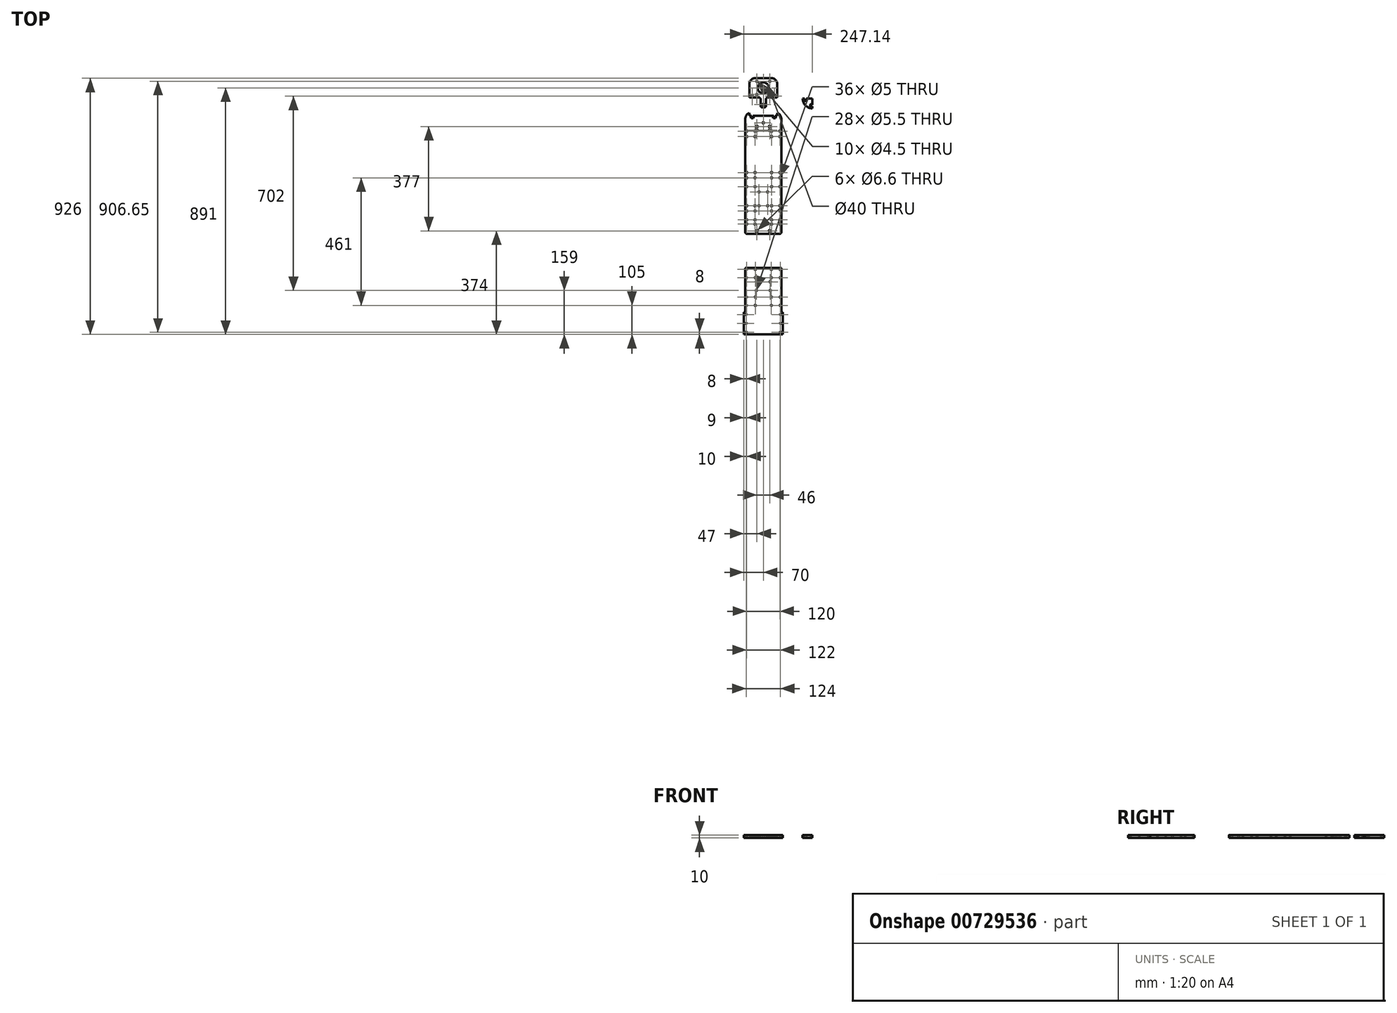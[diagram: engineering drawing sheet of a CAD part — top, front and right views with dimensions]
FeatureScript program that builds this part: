
annotation { "Feature Type Name" : "Feature", "Feature Type Description" : "" }
export const myFeature = defineFeature(function(context is Context, id is Id, definition is map)
    precondition{}
    {
        {
            var Q0;
            Q0=qCreatedBy(makeId("Top.planeOp"),FACE);
            var sketch = newSketch(context, id + "F0", { "sketchPlane" : qUnion([Q0])});
            skLineSegment(sketch, "E0.bottom", {"start": v(-65, 200) * mm, "end": v(65, 200) * mm});
            skLineSegment(sketch, "E0.top", {"start": v(-65, -200) * mm, "end": v(65, -200) * mm});
            skLineSegment(sketch, "E0.left", {"start": v(-65, 200) * mm, "end": v(-65, -121) * mm});
            skLineSegment(sketch, "E0.right", {"start": v(65, 200) * mm, "end": v(65, -121) * mm});
            skLineSegment(sketch, "E1", {"start": v(0, 0) * mm, "end": v(370.23, 0) * mm, "construction": true});
            skLineSegment(sketch, "E2", {"start": v(0, 0) * mm, "end": v(0, -200) * mm, "construction": true});
            skLineSegment(sketch, "E3", {"start": v(45, 0) * mm, "end": v(45, -60) * mm, "construction": true});
            skLineSegment(sketch, "E4", {"start": v(45, -60) * mm, "end": v(30.89, -60) * mm, "construction": true});
            skLineSegment(sketch, "E5", {"start": v(45, -44) * mm, "end": v(30, -44) * mm, "construction": true});
            skCircle(sketch, "E6", {"center": v(30, -44) * mm, "radius": 2.5 * mm});
            skCircle(sketch, "E7.MirrorC", {"center": v(30, -76) * mm, "radius": 2.5 * mm});
            skCircle(sketch, "E8.MirrorC", {"center": v(60, -44) * mm, "radius": 2.5 * mm});
            skCircle(sketch, "E9.MirrorC", {"center": v(60, -76) * mm, "radius": 2.5 * mm});
            skCircle(sketch, "E10.MirrorC", {"center": v(30, 44) * mm, "radius": 2.5 * mm});
            skCircle(sketch, "E11.MirrorC", {"center": v(60, 44) * mm, "radius": 2.5 * mm});
            skCircle(sketch, "E12.MirrorC", {"center": v(60, 76) * mm, "radius": 2.5 * mm});
            skCircle(sketch, "E13.MirrorC", {"center": v(30, 76) * mm, "radius": 2.5 * mm});
            skCircle(sketch, "E14.MirrorC", {"center": v(-30, 76) * mm, "radius": 2.5 * mm});
            skCircle(sketch, "E15.MirrorC", {"center": v(-30, 44) * mm, "radius": 2.5 * mm});
            skCircle(sketch, "E16.MirrorC", {"center": v(-60, 76) * mm, "radius": 2.5 * mm});
            skCircle(sketch, "E17.MirrorC", {"center": v(-60, 44) * mm, "radius": 2.5 * mm});
            skCircle(sketch, "E18.MirrorC", {"center": v(-60, -44) * mm, "radius": 2.5 * mm});
            skCircle(sketch, "E19.MirrorC", {"center": v(-30, -44) * mm, "radius": 2.5 * mm});
            skCircle(sketch, "E20.MirrorC", {"center": v(-30, -76) * mm, "radius": 2.5 * mm});
            skCircle(sketch, "E21.MirrorC", {"center": v(-60, -76) * mm, "radius": 2.5 * mm});
            skLineSegment(sketch, "E22", {"start": v(-131.72, 0) * mm, "end": v(0, 0) * mm, "construction": true});
            skPoint(sketch, "E23.orphan", {"position": v(65, 0) * mm});
            skCircle(sketch, "E24", {"center": v(-60, -55) * mm, "radius": 2.75 * mm, "construction": true});
            skLineSegment(sketch, "E25", {"start": v(-60, -55) * mm, "end": v(-30, -55) * mm, "construction": true});
            skLineSegment(sketch, "E26", {"start": v(-45, -390) * mm, "end": v(-45, -55) * mm, "construction": true});
            skCircle(sketch, "E27.MirrorC", {"center": v(-30, -55) * mm, "radius": 2.75 * mm, "construction": true});
            skCircle(sketch, "E28.0.1.0", {"center": v(-60, 95) * mm, "radius": 2.75 * mm});
            skCircle(sketch, "E28.0.1.1", {"center": v(-30, 95) * mm, "radius": 2.75 * mm});
            skCircle(sketch, "E28.0.2.0", {"center": v(-60, 245) * mm, "radius": 2.75 * mm});
            skCircle(sketch, "E28.0.2.1", {"center": v(-30, 245) * mm, "radius": 2.75 * mm});
            skCircle(sketch, "E28.1.0.0", {"center": v(30, -55) * mm, "radius": 2.75 * mm, "construction": true});
            skCircle(sketch, "E28.1.0.1", {"center": v(60, -55) * mm, "radius": 2.75 * mm, "construction": true});
            skCircle(sketch, "E28.1.1.0", {"center": v(30, 95) * mm, "radius": 2.75 * mm});
            skCircle(sketch, "E28.1.1.1", {"center": v(60, 95) * mm, "radius": 2.75 * mm});
            skCircle(sketch, "E28.1.2.0", {"center": v(30, 245) * mm, "radius": 2.75 * mm});
            skCircle(sketch, "E28.1.2.1", {"center": v(60, 245) * mm, "radius": 2.75 * mm});
            skLineSegment(sketch, "E28.direction1", {"start": v(-60, -55) * mm, "end": v(30, -55) * mm, "construction": true});
            skLineSegment(sketch, "E28.direction2", {"start": v(-60, -55) * mm, "end": v(-60, 95) * mm, "construction": true});
            skLineSegment(sketch, "E29", {"start": v(-65, -200) * mm, "end": v(-65, -250) * mm, "construction": true});
            skLineSegment(sketch, "E30", {"start": v(65, -200) * mm, "end": v(65, -250) * mm, "construction": true});
            skLineSegment(sketch, "E31.bottom", {"start": v(-65, -250) * mm, "end": v(65, -250) * mm});
            skLineSegment(sketch, "E31.top", {"start": v(-65, -390) * mm, "end": v(65, -390) * mm});
            skLineSegment(sketch, "E31.left", {"start": v(-65, -250) * mm, "end": v(-65, -390) * mm});
            skLineSegment(sketch, "E31.right", {"start": v(65, -250) * mm, "end": v(65, -390) * mm});
            skLineSegment(sketch, "E32", {"start": v(-65, -320) * mm, "end": v(65, -320) * mm, "construction": true});
            skPoint(sketch, "E33.orphan", {"position": v(-45, -52) * mm});
            skLineSegment(sketch, "E34", {"start": v(-45, -270) * mm, "end": v(-55, -270) * mm, "construction": true});
            skCircle(sketch, "E35", {"center": v(-61, -255) * mm, "radius": 2.5 * mm});
            skCircle(sketch, "E36.MirrorC", {"center": v(-61, -285) * mm, "radius": 2.5 * mm});
            skCircle(sketch, "E37.MirrorC", {"center": v(-29, -255) * mm, "radius": 2.5 * mm});
            skCircle(sketch, "E38.MirrorC", {"center": v(-29, -285) * mm, "radius": 2.5 * mm});
            skLineSegment(sketch, "E39", {"start": v(0, -320) * mm, "end": v(0, -250) * mm, "construction": true});
            skCircle(sketch, "E40.MirrorC", {"center": v(-29, -355) * mm, "radius": 2.5 * mm});
            skCircle(sketch, "E41.MirrorC", {"center": v(-61, -355) * mm, "radius": 2.5 * mm});
            skCircle(sketch, "E42.MirrorC", {"center": v(-61, -385) * mm, "radius": 2.5 * mm});
            skCircle(sketch, "E43.MirrorC", {"center": v(-29, -385) * mm, "radius": 2.5 * mm});
            skCircle(sketch, "E44.MirrorC", {"center": v(29, -255) * mm, "radius": 2.5 * mm});
            skCircle(sketch, "E45.MirrorC", {"center": v(29, -285) * mm, "radius": 2.5 * mm});
            skCircle(sketch, "E46.MirrorC", {"center": v(61, -255) * mm, "radius": 2.5 * mm});
            skCircle(sketch, "E47.MirrorC", {"center": v(61, -285) * mm, "radius": 2.5 * mm});
            skCircle(sketch, "E48.MirrorC", {"center": v(29, -355) * mm, "radius": 2.5 * mm});
            skCircle(sketch, "E49.MirrorC", {"center": v(61, -355) * mm, "radius": 2.5 * mm});
            skCircle(sketch, "E50.MirrorC", {"center": v(61, -385) * mm, "radius": 2.5 * mm});
            skCircle(sketch, "E51.MirrorC", {"center": v(29, -385) * mm, "radius": 2.5 * mm});
            skLineSegment(sketch, "E52.top", {"start": v(-65, -490) * mm, "end": v(65, -490) * mm});
            skLineSegment(sketch, "E52.left", {"start": v(-65, -390) * mm, "end": v(-65, -490) * mm});
            skLineSegment(sketch, "E52.right", {"start": v(65, -390) * mm, "end": v(65, -490) * mm});
            skLineSegment(sketch, "E53.top", {"start": v(-55, 300) * mm, "end": v(55, 300) * mm});
            skLineSegment(sketch, "E53.left", {"start": v(-65, 200) * mm, "end": v(-65, 290) * mm});
            skLineSegment(sketch, "E53.right", {"start": v(65, 200) * mm, "end": v(65, 290) * mm});
            skLineSegment(sketch, "E54", {"start": v(-60, -126) * mm, "end": v(60, -126) * mm});
            skPoint(sketch, "E55.middle", {"position": v(0, 0) * mm});
            skLineSegment(sketch, "E56.bottom", {"start": v(15.5, 25) * mm, "end": v(-15.5, 25) * mm, "construction": true});
            skLineSegment(sketch, "E56.top", {"start": v(15.5, -25) * mm, "end": v(-15.5, -25) * mm, "construction": true});
            skLineSegment(sketch, "E56.left", {"start": v(15.5, 25) * mm, "end": v(15.5, -25) * mm, "construction": true});
            skLineSegment(sketch, "E56.right", {"start": v(-15.5, 25) * mm, "end": v(-15.5, -25) * mm, "construction": true});
            skCircle(sketch, "E57", {"center": v(-15.5, 25) * mm, "radius": 2.5 * mm});
            skPoint(sketch, "E58.orphan", {"position": v(-65, 0) * mm});
            skLineSegment(sketch, "E59", {"start": v(0, 0) * mm, "end": v(0, 25) * mm, "construction": true});
            skCircle(sketch, "E60.MirrorC", {"center": v(15.5, 25) * mm, "radius": 2.5 * mm});
            skCircle(sketch, "E61.MirrorC", {"center": v(15.5, -25) * mm, "radius": 2.5 * mm});
            skCircle(sketch, "E62.MirrorC", {"center": v(-15.5, -25) * mm, "radius": 2.5 * mm});
            skLineSegment(sketch, "E63.bottom", {"start": v(-30, 30) * mm, "end": v(30, 30) * mm, "construction": true});
            skLineSegment(sketch, "E63.top", {"start": v(-30, -30) * mm, "end": v(30, -30) * mm, "construction": true});
            skLineSegment(sketch, "E63.left", {"start": v(-30, 30) * mm, "end": v(-30, -30) * mm, "construction": true});
            skLineSegment(sketch, "E63.right", {"start": v(30, 30) * mm, "end": v(30, -30) * mm, "construction": true});
            skLineSegment(sketch, "E64", {"start": v(0, -116) * mm, "end": v(23, -116) * mm, "construction": true});
            skCircle(sketch, "E65", {"center": v(23, -116) * mm, "radius": 3.3 * mm});
            skCircle(sketch, "E66.MirrorC", {"center": v(-23, -116) * mm, "radius": 3.3 * mm});
            skCircle(sketch, "E67", {"center": v(-25, -300) * mm, "radius": 2.75 * mm});
            skCircle(sketch, "E68.0.1.0", {"center": v(-25, -331) * mm, "radius": 2.75 * mm});
            skCircle(sketch, "E68.1.0.0", {"center": v(25, -300) * mm, "radius": 2.75 * mm});
            skCircle(sketch, "E68.1.1.0", {"center": v(25, -331) * mm, "radius": 2.75 * mm});
            skLineSegment(sketch, "E68.direction1", {"start": v(-25, -300) * mm, "end": v(25, -300) * mm, "construction": true});
            skLineSegment(sketch, "E68.direction2", {"start": v(-25, -300) * mm, "end": v(-25, -331) * mm, "construction": true});
            skLineSegment(sketch, "E69.bottom", {"start": v(70, -490) * mm, "end": v(-70, -490) * mm});
            skLineSegment(sketch, "E69.top", {"start": v(70, -410) * mm, "end": v(-70, -410) * mm});
            skLineSegment(sketch, "E69.left", {"start": v(70, -490) * mm, "end": v(70, -410) * mm});
            skLineSegment(sketch, "E69.right", {"start": v(-70, -490) * mm, "end": v(-70, -410) * mm});
            skPoint(sketch, "E69.middle", {"position": v(0, -450) * mm});
            skLineSegment(sketch, "E70", {"start": v(0, 235) * mm, "end": v(0, 333) * mm, "construction": true});
            skLineSegment(sketch, "E71", {"start": v(-65, 235) * mm, "end": v(65, 235) * mm, "construction": true});
            skCircle(sketch, "E72.MirrorC", {"center": v(-60, 225) * mm, "radius": 2.75 * mm});
            skCircle(sketch, "E73.MirrorC", {"center": v(-30, 225) * mm, "radius": 2.75 * mm});
            skCircle(sketch, "E74.MirrorC", {"center": v(30, 225) * mm, "radius": 2.75 * mm});
            skCircle(sketch, "E75.MirrorC", {"center": v(60, 225) * mm, "radius": 2.75 * mm});
            skLineSegment(sketch, "E76.bottom", {"start": v(50, 366) * mm, "end": v(15, 366) * mm});
            skLineSegment(sketch, "E76.top", {"start": v(30, 436) * mm, "end": v(-30, 436) * mm});
            skLineSegment(sketch, "E76.left", {"start": v(50, 366) * mm, "end": v(50, 416) * mm});
            skLineSegment(sketch, "E76.right", {"start": v(-50, 366) * mm, "end": v(-50, 416) * mm});
            skPoint(sketch, "E76.middle", {"position": v(0, 401) * mm});
            skCircle(sketch, "E77", {"center": v(0, 401) * mm, "radius": 20 * mm});
            skLineSegment(sketch, "E78.bottom", {"start": v(-23.65, 424.65) * mm, "end": v(23.65, 424.65) * mm, "construction": true});
            skLineSegment(sketch, "E78.top", {"start": v(-23.65, 377.35) * mm, "end": v(23.65, 377.35) * mm, "construction": true});
            skLineSegment(sketch, "E78.left", {"start": v(-23.65, 424.65) * mm, "end": v(-23.65, 377.35) * mm, "construction": true});
            skLineSegment(sketch, "E78.right", {"start": v(23.65, 424.65) * mm, "end": v(23.65, 377.35) * mm, "construction": true});
            skCircle(sketch, "E79", {"center": v(-23.65, 424.65) * mm, "radius": 2.25 * mm});
            skCircle(sketch, "E80", {"center": v(23.65, 424.65) * mm, "radius": 2.25 * mm});
            skCircle(sketch, "E81", {"center": v(-23.65, 377.35) * mm, "radius": 2.25 * mm});
            skCircle(sketch, "E82", {"center": v(23.65, 377.35) * mm, "radius": 2.25 * mm});
            skLineSegment(sketch, "E83", {"start": v(-40, 292) * mm, "end": v(-40, 300) * mm, "construction": true});
            skLineSegment(sketch, "E84", {"start": v(-40, 292) * mm, "end": v(-36.6, 292) * mm});
            skLineSegment(sketch, "E85", {"start": v(-36.6, 292) * mm, "end": v(-35, 293.6) * mm});
            skLineSegment(sketch, "E86", {"start": v(-35, 293.6) * mm, "end": v(-35, 296) * mm});
            skLineSegment(sketch, "E87", {"start": v(-35, 296) * mm, "end": v(-37, 296) * mm});
            skLineSegment(sketch, "E88", {"start": v(-37, 296) * mm, "end": v(-37, 300) * mm});
            skLineSegment(sketch, "E89", {"start": v(-37, 300) * mm, "end": v(-43, 300) * mm});
            skLineSegment(sketch, "E90", {"start": v(-42.5, 292) * mm, "end": v(-42.5, 300) * mm});
            skLineSegment(sketch, "E91.MirrorCS", {"start": v(-40, 292) * mm, "end": v(-43.4, 292) * mm});
            skLineSegment(sketch, "E92.MirrorCS", {"start": v(-37.5, 292) * mm, "end": v(-37.5, 300) * mm});
            skLineSegment(sketch, "E93.MirrorCS", {"start": v(-43, 300) * mm, "end": v(-37, 300) * mm});
            skLineSegment(sketch, "E94.MirrorCS", {"start": v(-43, 296) * mm, "end": v(-43, 300) * mm});
            skLineSegment(sketch, "E95.MirrorCS", {"start": v(-45, 296) * mm, "end": v(-43, 296) * mm});
            skLineSegment(sketch, "E96.MirrorCS", {"start": v(-45, 293.6) * mm, "end": v(-45, 296) * mm});
            skLineSegment(sketch, "E97.MirrorCS", {"start": v(-43.4, 292) * mm, "end": v(-45, 293.6) * mm});
            skLineSegment(sketch, "E98.MirrorCS", {"start": v(43, 296) * mm, "end": v(43, 300) * mm});
            skLineSegment(sketch, "E99.MirrorCS", {"start": v(45, 296) * mm, "end": v(43, 296) * mm});
            skLineSegment(sketch, "E100.MirrorCS", {"start": v(45, 293.6) * mm, "end": v(45, 296) * mm});
            skLineSegment(sketch, "E101.MirrorCS", {"start": v(43.4, 292) * mm, "end": v(45, 293.6) * mm});
            skLineSegment(sketch, "E102.MirrorCS", {"start": v(40, 292) * mm, "end": v(43.4, 292) * mm});
            skLineSegment(sketch, "E103.MirrorCS", {"start": v(40, 292) * mm, "end": v(36.6, 292) * mm});
            skLineSegment(sketch, "E104.MirrorCS", {"start": v(36.6, 292) * mm, "end": v(35, 293.6) * mm});
            skLineSegment(sketch, "E105.MirrorCS", {"start": v(35, 293.6) * mm, "end": v(35, 296) * mm});
            skLineSegment(sketch, "E106.MirrorCS", {"start": v(35, 296) * mm, "end": v(37, 296) * mm});
            skLineSegment(sketch, "E107.MirrorCS", {"start": v(37, 296) * mm, "end": v(37, 300) * mm});
            skPoint(sketch, "E108.visualSharp", {"position": v(-65, 300) * mm});
            skArc(sketch, "E108.filletArc", {"start": v(-55, 300) * mm, "mid": v(-62.07, 297.07) * mm, "end": v(-65, 290) * mm});
            skPoint(sketch, "E109.visualSharp", {"position": v(65, 300) * mm});
            skArc(sketch, "E109.filletArc", {"start": v(65, 290) * mm, "mid": v(62.07, 297.07) * mm, "end": v(55, 300) * mm});
            skLineSegment(sketch, "E110", {"start": v(-50, 371) * mm, "end": v(50, 371) * mm, "construction": true});
            skCircle(sketch, "E111", {"center": v(40, 371) * mm, "radius": 2.75 * mm});
            skCircle(sketch, "E112.MirrorC", {"center": v(-40, 371) * mm, "radius": 2.75 * mm});
            skLineSegment(sketch, "E113", {"start": v(50, 366) * mm, "end": v(50, 300) * mm, "construction": true});
            skLineSegment(sketch, "E114", {"start": v(50, 300) * mm, "end": v(50, 310) * mm});
            skArc(sketch, "E115", {"start": v(65, 290) * mm, "mid": v(60.83, 302.5) * mm, "end": v(50, 310) * mm});
            skLineSegment(sketch, "E116.MirrorCS", {"start": v(-50, 366) * mm, "end": v(-50, 300) * mm, "construction": true});
            skArc(sketch, "E117.MirrorCS", {"start": v(-65, 290) * mm, "mid": v(-60.83, 302.5) * mm, "end": v(-50, 310) * mm});
            skLineSegment(sketch, "E118.MirrorCS", {"start": v(-50, 300) * mm, "end": v(-50, 310) * mm});
            skPoint(sketch, "E119.orphan", {"position": v(0, 300) * mm});
            skCircle(sketch, "E120", {"center": v(0, 275) * mm, "radius": 2.75 * mm});
            skCircle(sketch, "E121", {"center": v(0, 341) * mm, "radius": 2.75 * mm});
            skPoint(sketch, "E122.visualSharp", {"position": v(-50, 436) * mm});
            skArc(sketch, "E122.filletArc", {"start": v(-30, 436) * mm, "mid": v(-44.14, 430.14) * mm, "end": v(-50, 416) * mm});
            skPoint(sketch, "E123.visualSharp", {"position": v(50, 436) * mm});
            skArc(sketch, "E123.filletArc", {"start": v(50, 416) * mm, "mid": v(44.14, 430.14) * mm, "end": v(30, 436) * mm});
            skLineSegment(sketch, "E124.trimOffspring", {"start": v(0, 333) * mm, "end": v(0, 388.53) * mm, "construction": true});
            skLineSegment(sketch, "E125.top", {"start": v(-5, 331) * mm, "end": v(5, 331) * mm});
            skLineSegment(sketch, "E125.left", {"start": v(-10, 361) * mm, "end": v(-10, 336) * mm});
            skLineSegment(sketch, "E125.right", {"start": v(10, 361) * mm, "end": v(10, 336) * mm});
            skPoint(sketch, "E125.middle", {"position": v(0, 348.5) * mm});
            skPoint(sketch, "E126.visualSharp", {"position": v(-10, 331) * mm});
            skArc(sketch, "E126.filletArc", {"start": v(-10, 336) * mm, "mid": v(-8.54, 332.46) * mm, "end": v(-5, 331) * mm});
            skPoint(sketch, "E127.visualSharp", {"position": v(10, 331) * mm});
            skArc(sketch, "E127.filletArc", {"start": v(5, 331) * mm, "mid": v(8.54, 332.46) * mm, "end": v(10, 336) * mm});
            skLineSegment(sketch, "E128.trimOffspring", {"start": v(-15, 366) * mm, "end": v(-50, 366) * mm});
            skPoint(sketch, "E129.visualSharp", {"position": v(-10, 366) * mm});
            skArc(sketch, "E129.filletArc", {"start": v(-10, 361) * mm, "mid": v(-11.46, 364.54) * mm, "end": v(-15, 366) * mm});
            skPoint(sketch, "E130.visualSharp", {"position": v(10, 366) * mm});
            skArc(sketch, "E130.filletArc", {"start": v(15, 366) * mm, "mid": v(11.46, 364.54) * mm, "end": v(10, 361) * mm});
            skLineSegment(sketch, "E131", {"start": v(152.14, 354.26) * mm, "end": v(152.14, 362.26) * mm, "construction": true});
            skLineSegment(sketch, "E132", {"start": v(152.14, 354.26) * mm, "end": v(155.54, 354.26) * mm});
            skLineSegment(sketch, "E133", {"start": v(155.54, 354.26) * mm, "end": v(157.14, 355.86) * mm});
            skLineSegment(sketch, "E134", {"start": v(157.14, 355.86) * mm, "end": v(157.14, 358.26) * mm});
            skLineSegment(sketch, "E135", {"start": v(157.14, 358.26) * mm, "end": v(155.14, 358.26) * mm});
            skLineSegment(sketch, "E136", {"start": v(155.14, 358.26) * mm, "end": v(155.14, 362.26) * mm});
            skLineSegment(sketch, "E137", {"start": v(155.14, 362.26) * mm, "end": v(149.14, 362.26) * mm});
            skLineSegment(sketch, "E138", {"start": v(149.64, 354.26) * mm, "end": v(149.64, 362.26) * mm});
            skLineSegment(sketch, "E139.MirrorCS", {"start": v(152.14, 354.26) * mm, "end": v(148.74, 354.26) * mm});
            skLineSegment(sketch, "E140.MirrorCS", {"start": v(154.64, 354.26) * mm, "end": v(154.64, 362.26) * mm});
            skLineSegment(sketch, "E141.MirrorCS", {"start": v(149.14, 362.26) * mm, "end": v(155.14, 362.26) * mm});
            skLineSegment(sketch, "E142.MirrorCS", {"start": v(149.14, 358.26) * mm, "end": v(149.14, 362.26) * mm});
            skLineSegment(sketch, "E143.MirrorCS", {"start": v(147.14, 358.26) * mm, "end": v(149.14, 358.26) * mm});
            skLineSegment(sketch, "E144.MirrorCS", {"start": v(147.14, 355.86) * mm, "end": v(147.14, 358.26) * mm});
            skLineSegment(sketch, "E145.MirrorCS", {"start": v(148.74, 354.26) * mm, "end": v(147.14, 355.86) * mm});
            skLineSegment(sketch, "E146", {"start": v(169.14, 337.26) * mm, "end": v(177.14, 337.26) * mm, "construction": true});
            skLineSegment(sketch, "E147", {"start": v(169.14, 337.26) * mm, "end": v(169.14, 333.86) * mm});
            skLineSegment(sketch, "E148", {"start": v(169.14, 333.86) * mm, "end": v(170.74, 332.26) * mm});
            skLineSegment(sketch, "E149", {"start": v(170.74, 332.26) * mm, "end": v(173.14, 332.26) * mm});
            skLineSegment(sketch, "E150", {"start": v(173.14, 332.26) * mm, "end": v(173.14, 334.26) * mm});
            skLineSegment(sketch, "E151", {"start": v(173.14, 334.26) * mm, "end": v(177.14, 334.26) * mm});
            skLineSegment(sketch, "E152", {"start": v(177.14, 334.26) * mm, "end": v(177.14, 340.26) * mm});
            skLineSegment(sketch, "E153", {"start": v(169.14, 339.76) * mm, "end": v(177.14, 339.76) * mm});
            skLineSegment(sketch, "E154.MirrorCS", {"start": v(169.14, 337.26) * mm, "end": v(169.14, 340.66) * mm});
            skLineSegment(sketch, "E155.MirrorCS", {"start": v(169.14, 334.76) * mm, "end": v(177.14, 334.76) * mm});
            skLineSegment(sketch, "E156.MirrorCS", {"start": v(177.14, 340.26) * mm, "end": v(177.14, 334.26) * mm});
            skLineSegment(sketch, "E157.MirrorCS", {"start": v(173.14, 340.26) * mm, "end": v(177.14, 340.26) * mm});
            skLineSegment(sketch, "E158.MirrorCS", {"start": v(173.14, 342.26) * mm, "end": v(173.14, 340.26) * mm});
            skLineSegment(sketch, "E159.MirrorCS", {"start": v(170.74, 342.26) * mm, "end": v(173.14, 342.26) * mm});
            skLineSegment(sketch, "E160.MirrorCS", {"start": v(169.14, 340.66) * mm, "end": v(170.74, 342.26) * mm});
            skLineSegment(sketch, "E161", {"start": v(155.14, 362.26) * mm, "end": v(177.14, 362.26) * mm});
            skLineSegment(sketch, "E162", {"start": v(177.14, 362.26) * mm, "end": v(177.14, 340.26) * mm});
            skLineSegment(sketch, "E163", {"start": v(149.14, 362.26) * mm, "end": v(142.14, 362.26) * mm});
            skLineSegment(sketch, "E164", {"start": v(177.14, 334.26) * mm, "end": v(177.14, 327.26) * mm});
            skArc(sketch, "E165", {"start": v(142.14, 362.26) * mm, "mid": v(152.39, 337.51) * mm, "end": v(177.14, 327.26) * mm});
            skLineSegment(sketch, "E166", {"start": v(-65, -91) * mm, "end": v(65, -91) * mm, "construction": true});
            skLineSegment(sketch, "E167", {"start": v(-8.26, -55) * mm, "end": v(-8.26, -91) * mm, "construction": true});
            skLineSegment(sketch, "E168", {"start": v(-8.26, -73) * mm, "end": v(-15.16, -73) * mm, "construction": true});
            skCircle(sketch, "E169.MirrorC", {"center": v(-30, -91) * mm, "radius": 2.75 * mm});
            skCircle(sketch, "E170.MirrorC", {"center": v(-60, -91) * mm, "radius": 2.75 * mm});
            skCircle(sketch, "E171.MirrorC", {"center": v(30, -91) * mm, "radius": 2.75 * mm});
            skCircle(sketch, "E172.MirrorC", {"center": v(60, -91) * mm, "radius": 2.75 * mm});
            skLineSegment(sketch, "E173", {"start": v(-65, -40) * mm, "end": v(65, -40) * mm, "construction": true});
            skCircle(sketch, "E174.MirrorC", {"center": v(-60, -25) * mm, "radius": 2.75 * mm});
            skCircle(sketch, "E175.MirrorC", {"center": v(-30, -25) * mm, "radius": 2.75 * mm});
            skCircle(sketch, "E176.MirrorC", {"center": v(30, -25) * mm, "radius": 2.75 * mm});
            skCircle(sketch, "E177.MirrorC", {"center": v(60, -25) * mm, "radius": 2.75 * mm});
            skPoint(sketch, "E178.visualSharp", {"position": v(-65, -126) * mm});
            skArc(sketch, "E178.filletArc", {"start": v(-65, -121) * mm, "mid": v(-63.54, -124.54) * mm, "end": v(-60, -126) * mm});
            skPoint(sketch, "E179.visualSharp", {"position": v(65, -126) * mm});
            skArc(sketch, "E179.filletArc", {"start": v(60, -126) * mm, "mid": v(63.54, -124.54) * mm, "end": v(65, -121) * mm});
            skCircle(sketch, "E180", {"center": v(-62, -482) * mm, "radius": 2.25 * mm});
            skCircle(sketch, "E181.0.1.0", {"center": v(-62, -450) * mm, "radius": 2.25 * mm});
            skCircle(sketch, "E181.0.2.0", {"center": v(-62, -418) * mm, "radius": 2.25 * mm});
            skLineSegment(sketch, "E181.direction1", {"start": v(-62, -482) * mm, "end": v(-35, -482) * mm, "construction": true});
            skLineSegment(sketch, "E181.direction2", {"start": v(-62, -482) * mm, "end": v(-62, -450) * mm, "construction": true});
            skCircle(sketch, "E182.MirrorC", {"center": v(62, -418) * mm, "radius": 2.25 * mm});
            skCircle(sketch, "E183.MirrorC", {"center": v(62, -450) * mm, "radius": 2.25 * mm});
            skCircle(sketch, "E184.MirrorC", {"center": v(62, -482) * mm, "radius": 2.25 * mm});
            skLineSegment(sketch, "E185", {"start": v(-23, 261) * mm, "end": v(23, 261) * mm, "construction": true});
            skCircle(sketch, "E186", {"center": v(-23, 261) * mm, "radius": 3.3 * mm});
            skCircle(sketch, "E187.MirrorC", {"center": v(23, 261) * mm, "radius": 3.3 * mm});
            skLineSegment(sketch, "E188", {"start": v(0, 248) * mm, "end": v(23, 248) * mm, "construction": true});
            skCircle(sketch, "E189", {"center": v(23, 248) * mm, "radius": 3.3 * mm});
            skCircle(sketch, "E190.MirrorC", {"center": v(-23, 248) * mm, "radius": 3.3 * mm});
            skSolve(sketch);
        }
        {
            var Q0;
            Q0=makeQuery(id+"F0.imprint","IMPRINT",FACE,{"disambiguationData":[TD([[makeQuery(id+"F0.imprint","IMPRINT",EDGE,{"derivedFrom":sQuery(id+"F0.wireOp",EDGE,"E0.bottom")}),-1.0]])]});
            var Q1;
            Q1=makeQuery(id+"F0.imprint","IMPRINT",FACE,{"disambiguationData":[TD([[makeQuery(id+"F0.imprint","IMPRINT",EDGE,{"derivedFrom":sQuery(id+"F0.wireOp",EDGE,"E0.bottom")}),1.0]])]});
            var Q2;
            Q2=makeQuery(id+"F0.imprint","IMPRINT",FACE,{"disambiguationData":[TD([[makeQuery(id+"F0.imprint","IMPRINT",EDGE,{"derivedFrom":sQuery(id+"F0.wireOp",EDGE,"E0.bottom")}),-1.0]])]});
            var Q3;
            {var subQ5=sQuery(id+"F0.wireOp",EDGE,"E63.right");Q3=makeQuery(id+"F0.imprint","IMPRINT",FACE,{"disambiguationData":[TD([[makeQuery(id+"F0.imprint","IMPRINT",EDGE,{"derivedFrom":subQ5}),-1.0]])]});}
            var Q4;
            {var subQ0=sQuery(id+"F0.wireOp",EDGE,"E108.filletArc");Q4=makeQuery(id+"F0.imprint","IMPRINT",FACE,{"disambiguationData":[TD([[makeQuery(id+"F0.imprint","IMPRINT",EDGE,{"derivedFrom":subQ0}),-1.0]])]});}
            var Q5;
            {var subQ0=sQuery(id+"F0.wireOp",EDGE,"E109.filletArc");Q5=makeQuery(id+"F0.imprint","IMPRINT",FACE,{"disambiguationData":[TD([[makeQuery(id+"F0.imprint","IMPRINT",EDGE,{"derivedFrom":subQ0}),-1.0]])]});}
            extrude(context, id + "F1", {"entities" : qUnion([Q0, Q1, Q2, Q3, Q4, Q5]), "depth" : 10 * mm, "offsetDistance" : 25 * mm});
        }
        {
            var Q0;
            Q0=makeQuery(id+"F0.imprint","IMPRINT",FACE,{"disambiguationData":[TD([[makeQuery(id+"F0.imprint","IMPRINT",EDGE,{"derivedFrom":sQuery(id+"F0.wireOp",EDGE,"E31.bottom")}),-1.0]])]});
            var Q1;
            {var subQ0=sQuery(id+"F0.wireOp",EDGE,"E31.top");Q1=makeQuery(id+"F0.imprint","IMPRINT",FACE,{"disambiguationData":[TD([[makeQuery(id+"F0.imprint","IMPRINT",EDGE,{"derivedFrom":subQ0}),-1.0]])]});}
            var Q2;
            {var subQ6=sQuery(id+"F0.wireOp",EDGE,"E52.top");Q2=makeQuery(id+"F0.imprint","IMPRINT",FACE,{"disambiguationData":[TD([[makeQuery(id+"F0.imprint","IMPRINT",EDGE,{"derivedFrom":subQ6}),1.0]])]});}
            var Q3;
            {var subQ5=sQuery(id+"F0.wireOp",EDGE,"E69.right");Q3=makeQuery(id+"F0.imprint","IMPRINT",FACE,{"disambiguationData":[TD([[makeQuery(id+"F0.imprint","IMPRINT",EDGE,{"derivedFrom":subQ5}),-1.0]])]});}
            var Q4;
            {var subQ5=sQuery(id+"F0.wireOp",EDGE,"E69.left");Q4=makeQuery(id+"F0.imprint","IMPRINT",FACE,{"disambiguationData":[TD([[makeQuery(id+"F0.imprint","IMPRINT",EDGE,{"derivedFrom":subQ5}),1.0]])]});}
            extrude(context, id + "F2", {"entities" : qUnion([Q0, Q1, Q2, Q3, Q4]), "depth" : 10 * mm, "offsetDistance" : 25 * mm});
        }
        {
            var Q0;
            Q0=makeQuery(id+"F0.imprint","IMPRINT",FACE,{"disambiguationData":[TD([[makeQuery(id+"F0.imprint","IMPRINT",EDGE,{"derivedFrom":sQuery(id+"F0.wireOp",EDGE,"E76.bottom")}),-1.0]])]});
            var Q1;
            Q1=makeQuery(id+"F0.imprint","IMPRINT",FACE,{"disambiguationData":[TD([[makeQuery(id+"F0.imprint","IMPRINT",EDGE,{"derivedFrom":sQuery(id+"F0.wireOp",EDGE,"iVLYcmu8-LmAy-dfAt-mDo3-UHBj7ujcx1AR.bottom")}),-1.0]])]});
            extrude(context, id + "F3", {"entities" : qUnion([Q0, Q1]), "depth" : 10 * mm, "offsetDistance" : 25 * mm});
        }
        {
            var Q0;
            {var subQ6=sQuery(id+"F0.wireOp",EDGE,"E133");Q0=makeQuery(id+"F0.imprint","IMPRINT",FACE,{"disambiguationData":[TD([[makeQuery(id+"F0.imprint","IMPRINT",EDGE,{"derivedFrom":subQ6}),-1.0]])]});}
            extrude(context, id + "F4", {"entities" : qUnion([Q0]), "depth" : 10 * mm, "offsetDistance" : 25 * mm});
        }
    });
